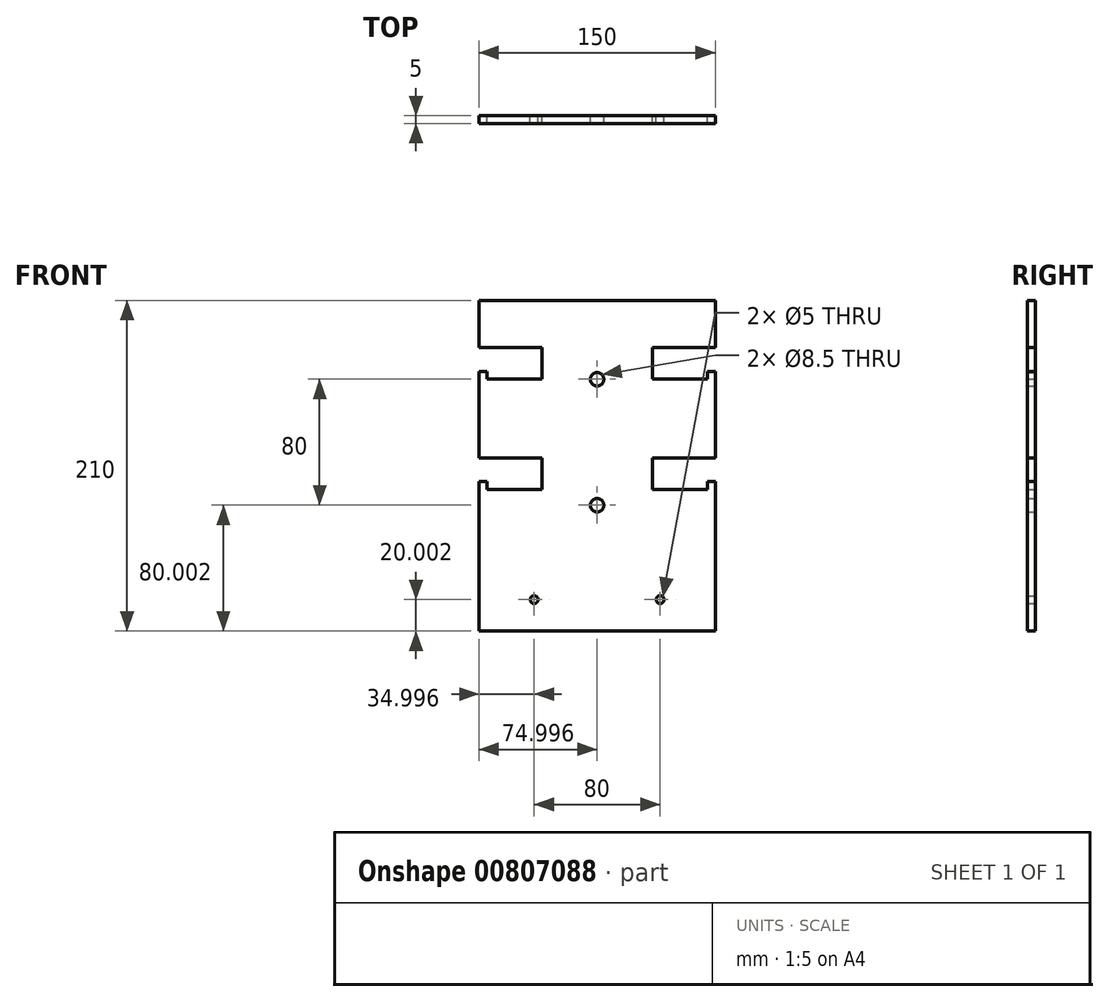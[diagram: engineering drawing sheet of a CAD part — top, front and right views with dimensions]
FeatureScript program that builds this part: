
annotation { "Feature Type Name" : "Feature", "Feature Type Description" : "" }
export const myFeature = defineFeature(function(context is Context, id is Id, definition is map)
    precondition{}
    {
        {
            var Q0;
            Q0=qCreatedBy(makeId("Front.planeOp"),FACE);
            var sketch = newSketch(context, id + "F0", { "sketchPlane" : qUnion([Q0])});
            skLineSegment(sketch, "E0.bottom", {"start": v(-70.13, 127.27) * mm, "end": v(79.87, 127.27) * mm});
            skLineSegment(sketch, "E0.top", {"start": v(-70.13, -82.73) * mm, "end": v(79.87, -82.73) * mm});
            skLineSegment(sketch, "E0.left", {"start": v(-70.13, 127.27) * mm, "end": v(-70.13, -82.73) * mm});
            skLineSegment(sketch, "E0.right", {"start": v(79.87, 127.27) * mm, "end": v(79.87, -82.73) * mm});
            skLineSegment(sketch, "E1", {"start": v(-70.13, -62.73) * mm, "end": v(79.87, -62.73) * mm, "construction": true});
            skCircle(sketch, "E2", {"center": v(-35.13, -62.73) * mm, "radius": 2.5 * mm});
            skCircle(sketch, "E3", {"center": v(44.87, -62.73) * mm, "radius": 2.5 * mm});
            skLineSegment(sketch, "E4", {"start": v(-65.13, 7.27) * mm, "end": v(74.87, 7.27) * mm});
            skLineSegment(sketch, "E5.bottom", {"start": v(-70.13, 27.27) * mm, "end": v(-30.13, 27.27) * mm});
            skLineSegment(sketch, "E5.top", {"start": v(-65.13, 7.27) * mm, "end": v(-30.13, 7.27) * mm});
            skLineSegment(sketch, "E5.left", {"start": v(-70.13, 27.27) * mm, "end": v(-70.13, 12.27) * mm});
            skLineSegment(sketch, "E5.right", {"start": v(-30.13, 27.27) * mm, "end": v(-30.13, 7.27) * mm});
            skLineSegment(sketch, "E6.bottom", {"start": v(-70.13, 12.27) * mm, "end": v(-65.13, 12.27) * mm});
            skLineSegment(sketch, "E6.right", {"start": v(-65.13, 12.27) * mm, "end": v(-65.13, 7.27) * mm});
            skLineSegment(sketch, "E7", {"start": v(4.87, 127.27) * mm, "end": v(4.87, -82.73) * mm, "construction": true});
            skLineSegment(sketch, "E8.MirrorCS", {"start": v(79.87, 27.27) * mm, "end": v(39.87, 27.27) * mm});
            skLineSegment(sketch, "E9.MirrorCS", {"start": v(39.87, 27.27) * mm, "end": v(39.87, 7.27) * mm});
            skLineSegment(sketch, "E10.MirrorCS", {"start": v(74.87, 7.27) * mm, "end": v(39.87, 7.27) * mm});
            skLineSegment(sketch, "E11.MirrorCS", {"start": v(79.87, 12.27) * mm, "end": v(74.87, 12.27) * mm});
            skLineSegment(sketch, "E12.MirrorCS", {"start": v(79.87, 27.27) * mm, "end": v(79.87, 12.27) * mm});
            skLineSegment(sketch, "E13.MirrorCS", {"start": v(74.87, 12.27) * mm, "end": v(74.87, 7.27) * mm});
            skLineSegment(sketch, "E14", {"start": v(-70.13, 57.27) * mm, "end": v(79.87, 57.27) * mm, "construction": true});
            skLineSegment(sketch, "E15.MirrorCS", {"start": v(79.87, -12.73) * mm, "end": v(79.87, 197.27) * mm});
            skLineSegment(sketch, "E16.bottom", {"start": v(-65.13, 77.27) * mm, "end": v(-30.13, 77.27) * mm});
            skLineSegment(sketch, "E16.top", {"start": v(-70.13, 97.27) * mm, "end": v(-30.13, 97.27) * mm});
            skLineSegment(sketch, "E16.left", {"start": v(-70.13, 82.27) * mm, "end": v(-70.13, 97.27) * mm});
            skLineSegment(sketch, "E16.right", {"start": v(-30.13, 77.27) * mm, "end": v(-30.13, 97.27) * mm});
            skLineSegment(sketch, "E17.bottom", {"start": v(-70.13, 82.27) * mm, "end": v(-65.13, 82.27) * mm});
            skLineSegment(sketch, "E17.right", {"start": v(-65.13, 82.27) * mm, "end": v(-65.13, 77.27) * mm});
            skLineSegment(sketch, "E18.MirrorCS", {"start": v(74.87, 77.27) * mm, "end": v(39.87, 77.27) * mm});
            skLineSegment(sketch, "E19.MirrorCS", {"start": v(39.87, 77.27) * mm, "end": v(39.87, 97.27) * mm});
            skLineSegment(sketch, "E20.MirrorCS", {"start": v(79.87, 97.27) * mm, "end": v(39.87, 97.27) * mm});
            skLineSegment(sketch, "E21.MirrorCS", {"start": v(79.87, 82.27) * mm, "end": v(74.87, 82.27) * mm});
            skLineSegment(sketch, "E22.MirrorCS", {"start": v(74.87, 82.27) * mm, "end": v(74.87, 77.27) * mm});
            skCircle(sketch, "E23", {"center": v(4.87, -2.73) * mm, "radius": 4.25 * mm});
            skCircle(sketch, "E24", {"center": v(4.87, 77.27) * mm, "radius": 4.25 * mm});
            skSolve(sketch);
        }
        {
            var Q0;
            {var subQ7=sQuery(id+"F0.wireOp",EDGE,"E5.bottom");Q0=makeQuery(id+"F0.imprint","IMPRINT",FACE,{"disambiguationData":[TD([[makeQuery(id+"F0.imprint","IMPRINT",EDGE,{"derivedFrom":subQ7}),1.0]])]});}
            var Q1;
            {var subQ0=sQuery(id+"F0.wireOp",EDGE,"E8.MirrorCS");Q1=makeQuery(id+"F0.imprint","IMPRINT",FACE,{"disambiguationData":[TD([[makeQuery(id+"F0.imprint","IMPRINT",EDGE,{"derivedFrom":subQ0}),-1.0]])]});}
            var Q2;
            Q2=makeQuery(id+"F0.imprint","IMPRINT",FACE,{"disambiguationData":[TD([[makeQuery(id+"F0.imprint","IMPRINT",EDGE,{"derivedFrom":sQuery(id+"F0.wireOp",EDGE,"E3")}),-1.0]])]});
            var Q3;
            Q3=makeQuery(id+"F0.imprint","IMPRINT",FACE,{"disambiguationData":[TD([[makeQuery(id+"F0.imprint","IMPRINT",EDGE,{"derivedFrom":sQuery(id+"F0.wireOp",EDGE,"E2")}),-1.0]])]});
            extrude(context, id + "F1", {"entities" : qUnion([Q0, Q1, Q2, Q3]), "depth" : 5 * mm, "offsetDistance" : 25 * mm});
        }
    });
